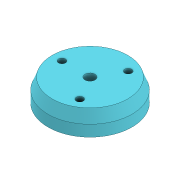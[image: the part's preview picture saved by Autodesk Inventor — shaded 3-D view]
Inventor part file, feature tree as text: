
AUTODESK INVENTOR PART (.ipt)
format: ipt  version: 2020.3 (Build 243373000, 373)  size: 105,472 bytes
history: native  units: mm
features: extrude x1, chamfer x1, sketch x1
ambient origin geometry x8: Origin, YZ Plane, XZ Plane, XY Plane, X Axis, Y Axis, Z Axis, Center Point
bodies: Solid1 (feature_tree)
feature tree (3):
  extrude  "Extrusion1"  Depth=10.0mm
  chamfer  "Chamfer1"  Distance=2.5mm
  sketch  "Sketch1"  dims[d1=3.6mm d2=30.0mm d3=8.660254mm d4=10.0mm d5=10.0mm d6=10.0mm d7=2.5mm d8=2.5mm d9=2.5mm d10=8.0mm d11=0.0mm d12=1.5mm d13=4.0mm d14=45.0deg]
